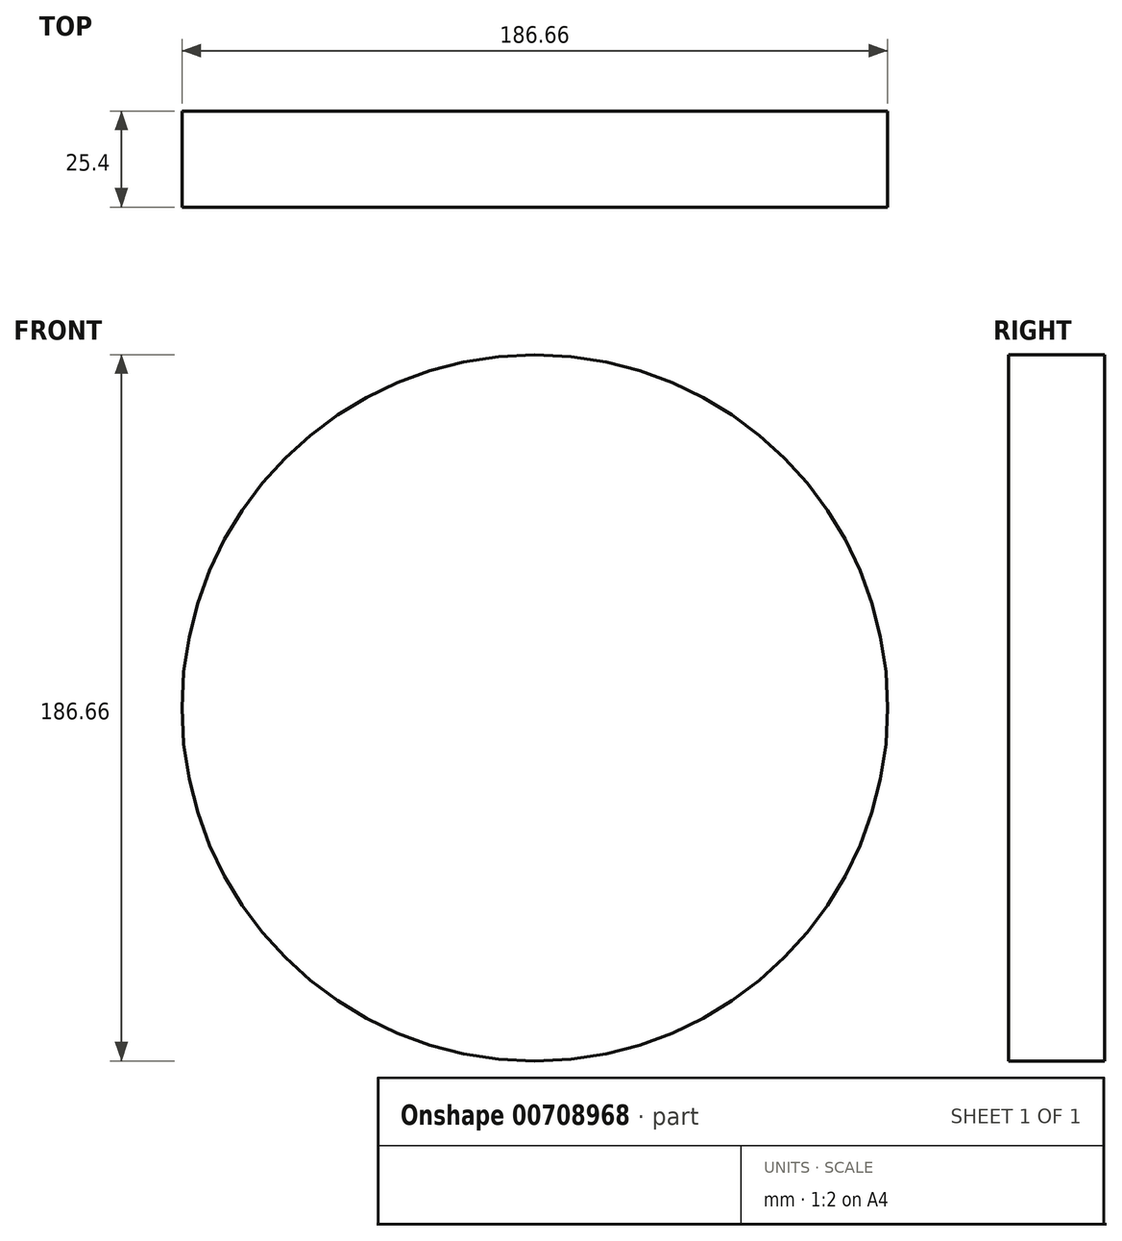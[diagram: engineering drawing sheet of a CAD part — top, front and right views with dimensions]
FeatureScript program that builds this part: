
annotation { "Feature Type Name" : "Feature", "Feature Type Description" : "" }
export const myFeature = defineFeature(function(context is Context, id is Id, definition is map)
    precondition{}
    {
        {
            var Q0;
            Q0=qCreatedBy(makeId("Front.planeOp"),FACE);
            var sketch = newSketch(context, id + "F0", { "sketchPlane" : qUnion([Q0])});
            skCircle(sketch, "E0", {"center": v(0, 0) * mm, "radius": 93.33 * mm});
            skSolve(sketch);
        }
        {
            var Q0;
            Q0=makeQuery(id+"F0.imprint","IMPRINT",FACE,{"disambiguationData":[TD([[makeQuery(id+"F0.imprint","IMPRINT",EDGE,{"derivedFrom":sQuery(id+"F0.wireOp",EDGE,"E0")}),1.0]])]});
            extrude(context, id + "F1", {"entities" : qUnion([Q0]), "depth" : 25.4 * mm, "offsetDistance" : 25.4 * mm});
        }
    });
